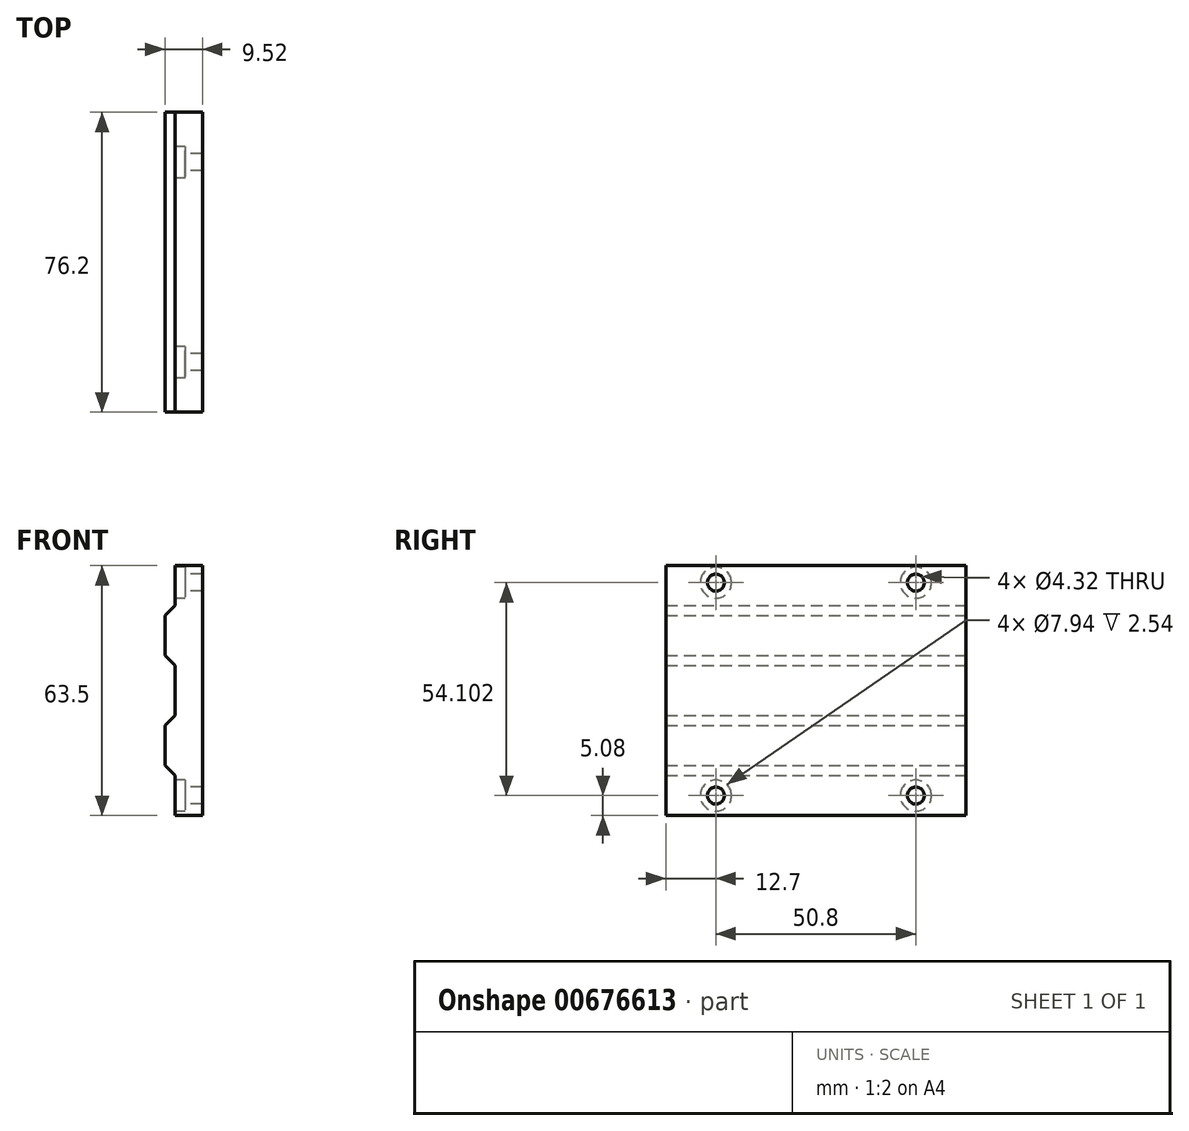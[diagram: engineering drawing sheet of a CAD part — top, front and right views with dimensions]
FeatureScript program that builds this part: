
annotation { "Feature Type Name" : "Feature", "Feature Type Description" : "" }
export const myFeature = defineFeature(function(context is Context, id is Id, definition is map)
    precondition{}
    {
        {
            var Q0;
            Q0=qCreatedBy(makeId("Front.planeOp"),FACE);
            var sketch = newSketch(context, id + "F0", { "sketchPlane" : qUnion([Q0])});
            skLineSegment(sketch, "E0.0.0", {"start": v(6.99, 40.64) * mm, "end": v(6.98, 50.8) * mm});
            skLineSegment(sketch, "E0.0.1", {"start": v(6.98, 50.8) * mm, "end": v(9.52, 53.34) * mm});
            skLineSegment(sketch, "E0.0.2", {"start": v(9.52, 53.34) * mm, "end": v(9.52, 63.5) * mm});
            skLineSegment(sketch, "E0.0.3", {"start": v(9.52, 63.5) * mm, "end": v(0, 63.5) * mm});
            skLineSegment(sketch, "E0.0.4", {"start": v(0, 63.5) * mm, "end": v(0, 0) * mm});
            skLineSegment(sketch, "E0.0.5", {"start": v(0, 0) * mm, "end": v(9.53, 0) * mm});
            skLineSegment(sketch, "E0.0.6", {"start": v(9.53, 0) * mm, "end": v(9.53, 10.16) * mm});
            skLineSegment(sketch, "E0.0.7", {"start": v(9.53, 10.16) * mm, "end": v(6.98, 12.7) * mm});
            skLineSegment(sketch, "E0.0.8", {"start": v(6.99, 12.7) * mm, "end": v(6.98, 22.86) * mm});
            skLineSegment(sketch, "E0.0.9", {"start": v(6.98, 22.86) * mm, "end": v(9.52, 25.4) * mm});
            skLineSegment(sketch, "E0.0.10", {"start": v(9.53, 25.4) * mm, "end": v(9.52, 38.1) * mm});
            skLineSegment(sketch, "E0.0.11", {"start": v(9.52, 38.1) * mm, "end": v(6.98, 40.64) * mm});
            skLineSegment(sketch, "E1", {"start": v(9.52, 63.5) * mm, "end": v(16.5, 63.5) * mm});
            skLineSegment(sketch, "E2", {"start": v(16.5, 63.5) * mm, "end": v(16.51, 0) * mm});
            skLineSegment(sketch, "E3", {"start": v(16.51, 0) * mm, "end": v(9.53, 0) * mm});
            skSolve(sketch);
        }
        {
            var Q0;
            Q0=makeQuery(id+"F0.imprint","IMPRINT",FACE,{"disambiguationData":[TD([[makeQuery(id+"F0.imprint","IMPRINT",EDGE,{"derivedFrom":sQuery(id+"F0.wireOp",EDGE,"E0.0.0")}),-1.0]])]});
            extrude(context, id + "F1", {"entities" : qUnion([Q0]), "depth" : 76.2 * mm});
        }
        {
            var Q0;
            Q0=makeQuery(id+"F1.opExtrude","SWEPT_FACE",FACE,{"disambiguationData":[OSD([sQuery(id+"F0.wireOp",EDGE,"E0.0.2")])]});
            var sketch = newSketch(context, id + "F2", { "sketchPlane" : qUnion([Q0])});
            skPoint(sketch, "E4", {"position": v(12.7, 59.18) * mm});
            skPoint(sketch, "E5", {"position": v(63.5, 59.18) * mm});
            skPoint(sketch, "E6", {"position": v(12.7, 5.08) * mm});
            skPoint(sketch, "E7", {"position": v(63.5, 5.08) * mm});
            skSolve(sketch);
        }
        {
            var Q0;
            Q0=sQuery(id+"F2.wireOp",VERTEX,"E6");
            var Q1;
            Q1=sQuery(id+"F2.wireOp",VERTEX,"E7");
            var Q2;
            Q2=makeQuery(id+"F1.opExtrude","SWEPT_BODY",BODY,{"disambiguationData":[OSD([sQuery(id+"F0.wireOp",EDGE,"E0.0.0"),sQuery(id+"F0.wireOp",EDGE,"E0.0.1"),sQuery(id+"F0.wireOp",EDGE,"E0.0.2"),sQuery(id+"F0.wireOp",EDGE,"E0.0.6"),sQuery(id+"F0.wireOp",EDGE,"E0.0.7"),sQuery(id+"F0.wireOp",EDGE,"E0.0.8"),sQuery(id+"F0.wireOp",EDGE,"E0.0.9"),sQuery(id+"F0.wireOp",EDGE,"E0.0.10"),sQuery(id+"F0.wireOp",EDGE,"E0.0.11"),sQuery(id+"F0.wireOp",EDGE,"E1"),sQuery(id+"F0.wireOp",EDGE,"E2"),sQuery(id+"F0.wireOp",EDGE,"E3")])]});
            hole(context, id + "F3", {"style" : HoleStyle.SIMPLE, "endStyle" : HoleEndStyle.BLIND, "standardTappedOrClearance" : lookupTablePath({ "standard" : "ANSI", "fit" : "Close", "size" : "#8", "type" : "Clearance" }), "standardBlindInLast" : lookupTablePath({ "fit" : "Close", "standard" : "ANSI", "size" : "#8", "type" : "Clearance" }), "holeDiameter" : 4.32 * mm, "majorDiameter" : 6.35 * mm, "holeDepth" : 12.7 * mm, "isTappedThrough" : true, "tappedDepth" : 10.32 * mm, "tapClearance" : 3, "locations" : qUnion([Q0, Q1]), "scope" : qUnion([Q2])});
        }
        {
            var Q0;
            Q0=sQuery(id+"F2.wireOp",VERTEX,"E4");
            var Q1;
            Q1=sQuery(id+"F2.wireOp",VERTEX,"E5");
            var Q2;
            Q2=makeQuery(id+"F1.opExtrude","SWEPT_BODY",BODY,{"disambiguationData":[OSD([sQuery(id+"F0.wireOp",EDGE,"E0.0.0"),sQuery(id+"F0.wireOp",EDGE,"E0.0.1"),sQuery(id+"F0.wireOp",EDGE,"E0.0.2"),sQuery(id+"F0.wireOp",EDGE,"E0.0.6"),sQuery(id+"F0.wireOp",EDGE,"E0.0.7"),sQuery(id+"F0.wireOp",EDGE,"E0.0.8"),sQuery(id+"F0.wireOp",EDGE,"E0.0.9"),sQuery(id+"F0.wireOp",EDGE,"E0.0.10"),sQuery(id+"F0.wireOp",EDGE,"E0.0.11"),sQuery(id+"F0.wireOp",EDGE,"E1"),sQuery(id+"F0.wireOp",EDGE,"E2"),sQuery(id+"F0.wireOp",EDGE,"E3")])]});
            hole(context, id + "F4", {"style" : HoleStyle.SIMPLE, "endStyle" : HoleEndStyle.BLIND, "standardTappedOrClearance" : lookupTablePath({ "standard" : "ANSI", "fit" : "Close", "size" : "#8", "type" : "Clearance" }), "standardBlindInLast" : lookupTablePath({ "fit" : "Close", "standard" : "ANSI", "size" : "#8", "type" : "Clearance" }), "holeDiameter" : 4.32 * mm, "majorDiameter" : 6.35 * mm, "holeDepth" : 12.7 * mm, "isTappedThrough" : true, "tappedDepth" : 10.32 * mm, "tapClearance" : 3, "locations" : qUnion([Q0, Q1]), "scope" : qUnion([Q2])});
        }
        {
            var Q0;
            Q0=makeQuery(id+"F1.opExtrude","SWEPT_FACE",FACE,{"disambiguationData":[OSD([sQuery(id+"F0.wireOp",EDGE,"E0.0.6")])]});
            var sketch = newSketch(context, id + "F5", { "sketchPlane" : qUnion([Q0])});
            skCircle(sketch, "E8", {"center": v(12.7, 5.08) * mm, "radius": 3.97 * mm});
            skCircle(sketch, "E9", {"center": v(63.5, 5.08) * mm, "radius": 3.97 * mm});
            skPoint(sketch, "E10.0", {"position": v(12.7, 59.18) * mm});
            skCircle(sketch, "E11", {"center": v(12.7, 59.18) * mm, "radius": 3.97 * mm});
            skPoint(sketch, "E12.0", {"position": v(63.5, 59.18) * mm});
            skCircle(sketch, "E13", {"center": v(63.5, 59.18) * mm, "radius": 3.97 * mm});
            skLineSegment(sketch, "E14.0.0", {"start": v(0, 63.5) * mm, "end": v(0, 53.34) * mm});
            skLineSegment(sketch, "E14.0.1", {"start": v(0, 53.34) * mm, "end": v(76.2, 53.34) * mm});
            skLineSegment(sketch, "E14.0.2", {"start": v(76.2, 53.34) * mm, "end": v(76.2, 63.5) * mm});
            skLineSegment(sketch, "E14.0.3", {"start": v(76.2, 63.5) * mm, "end": v(0, 63.5) * mm});
            skCircle(sketch, "E15.0", {"center": v(12.7, 59.18) * mm, "radius": 2.16 * mm});
            skCircle(sketch, "E16.0", {"center": v(63.5, 59.18) * mm, "radius": 2.16 * mm});
            skSolve(sketch);
        }
        {
            var Q0;
            Q0=makeQuery(id+"F5.imprint","IMPRINT",FACE,{"disambiguationData":[TD([[makeQuery(id+"F5.imprint","IMPRINT",EDGE,{"derivedFrom":sQuery(id+"F5.wireOp",EDGE,"E8")}),1.0]])]});
            var Q1;
            Q1=makeQuery(id+"F5.imprint","IMPRINT",FACE,{"disambiguationData":[TD([[makeQuery(id+"F5.imprint","IMPRINT",EDGE,{"derivedFrom":sQuery(id+"F5.wireOp",EDGE,"E9")}),1.0]])]});
            extrude(context, id + "F6", {"entities" : qUnion([Q0, Q1]), "operationType" : NewBodyOperationType.REMOVE, "oppositeDirection" : true, "depth" : 2.54 * mm, "offsetDistance" : 25.4 * mm});
        }
        {
            var Q0;
            Q0=makeQuery(id+"F5.imprint","IMPRINT",FACE,{"disambiguationData":[TD([[makeQuery(id+"F5.imprint","IMPRINT",EDGE,{"derivedFrom":sQuery(id+"F5.wireOp",EDGE,"E11")}),1.0]])]});
            var Q1;
            Q1=makeQuery(id+"F5.imprint","IMPRINT",FACE,{"disambiguationData":[TD([[makeQuery(id+"F5.imprint","IMPRINT",EDGE,{"derivedFrom":sQuery(id+"F5.wireOp",EDGE,"E13")}),1.0]])]});
            extrude(context, id + "F7", {"entities" : qUnion([Q0, Q1]), "operationType" : NewBodyOperationType.REMOVE, "oppositeDirection" : true, "depth" : 2.54 * mm, "offsetDistance" : 25.4 * mm});
        }
    });
